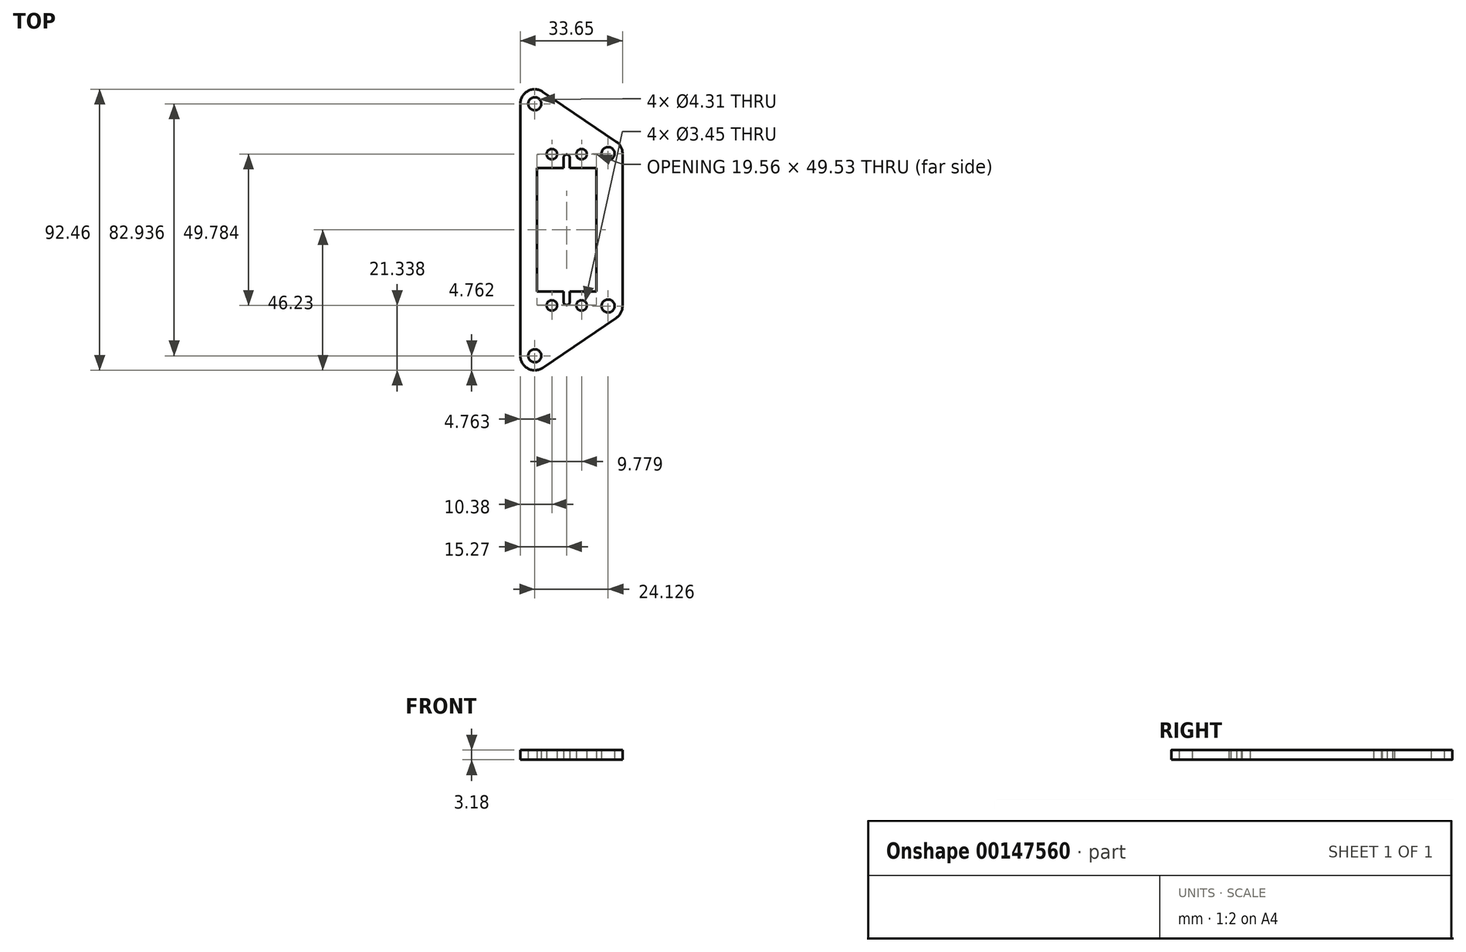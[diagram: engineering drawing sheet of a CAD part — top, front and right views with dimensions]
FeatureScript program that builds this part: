
annotation { "Feature Type Name" : "Feature", "Feature Type Description" : "" }
export const myFeature = defineFeature(function(context is Context, id is Id, definition is map)
    precondition{}
    {
        {
            var Q0;
            Q0=qCreatedBy(makeId("Top.planeOp"),FACE);
            var sketch = newSketch(context, id + "F0", { "sketchPlane" : qUnion([Q0])});
            skLineSegment(sketch, "E0.rect.bottom", {"start": v(-9.78, -20.32) * mm, "end": v(-9.78, 20.32) * mm});
            skLineSegment(sketch, "E0.rect.top", {"start": v(9.78, -20.32) * mm, "end": v(9.78, 20.32) * mm});
            skPoint(sketch, "E0.rect.middle", {"position": v(0, 0) * mm});
            skLineSegment(sketch, "E1.rect.bottom", {"start": v(-4.89, -24.9) * mm, "end": v(-4.89, 24.9) * mm, "construction": true});
            skLineSegment(sketch, "E1.rect.top", {"start": v(4.89, -24.9) * mm, "end": v(4.89, 24.9) * mm, "construction": true});
            skLineSegment(sketch, "E1.rect.left", {"start": v(-4.89, -24.9) * mm, "end": v(4.89, -24.9) * mm, "construction": true});
            skLineSegment(sketch, "E1.rect.right", {"start": v(-4.89, 24.9) * mm, "end": v(4.89, 24.9) * mm, "construction": true});
            skCircle(sketch, "E2", {"center": v(4.89, 24.9) * mm, "radius": 1.73 * mm});
            skCircle(sketch, "E3", {"center": v(-4.89, 24.9) * mm, "radius": 1.73 * mm});
            skCircle(sketch, "E4", {"center": v(4.89, -24.9) * mm, "radius": 1.73 * mm});
            skCircle(sketch, "E5", {"center": v(-4.89, -24.9) * mm, "radius": 1.73 * mm});
            skLineSegment(sketch, "E6", {"start": v(-9.78, 20.32) * mm, "end": v(-1.02, 20.32) * mm});
            skLineSegment(sketch, "E7", {"start": v(-1.02, 20.32) * mm, "end": v(-1.02, 23.75) * mm});
            skLineSegment(sketch, "E8", {"start": v(-1.02, 23.75) * mm, "end": v(1.02, 23.75) * mm, "construction": true});
            skLineSegment(sketch, "E9", {"start": v(1.02, 23.75) * mm, "end": v(1.02, 20.32) * mm});
            skLineSegment(sketch, "E10", {"start": v(1.02, 20.32) * mm, "end": v(9.78, 20.32) * mm});
            skLineSegment(sketch, "E11", {"start": v(9.78, -20.32) * mm, "end": v(1.02, -20.32) * mm});
            skLineSegment(sketch, "E12", {"start": v(1.02, -20.32) * mm, "end": v(1.02, -23.75) * mm});
            skLineSegment(sketch, "E13", {"start": v(1.02, -23.75) * mm, "end": v(-1.02, -23.75) * mm, "construction": true});
            skLineSegment(sketch, "E14", {"start": v(-1.02, -23.75) * mm, "end": v(-1.02, -20.32) * mm});
            skLineSegment(sketch, "E15", {"start": v(-1.02, -20.32) * mm, "end": v(-9.78, -20.32) * mm});
            skArc(sketch, "E16", {"start": v(1.02, 23.75) * mm, "mid": v(0, 24.77) * mm, "end": v(-1.02, 23.75) * mm});
            skArc(sketch, "E17", {"start": v(-1.02, -23.75) * mm, "mid": v(0, -24.76) * mm, "end": v(1.02, -23.75) * mm});
            skLineSegment(sketch, "E18", {"start": v(-1.02, 20.32) * mm, "end": v(1.02, 20.32) * mm, "construction": true});
            skLineSegment(sketch, "E19", {"start": v(0, 20.32) * mm, "end": v(0, 10.9) * mm, "construction": true});
            skLineSegment(sketch, "E20", {"start": v(0, 0) * mm, "end": v(0, 0) * mm});
            skLineSegment(sketch, "E21", {"start": v(13.62, 20.32) * mm, "end": v(13.62, 25.08) * mm, "construction": true});
            skLineSegment(sketch, "E22", {"start": v(9.78, 0) * mm, "end": v(18.38, 0) * mm, "construction": true});
            skCircle(sketch, "E23", {"center": v(13.62, 25.08) * mm, "radius": 2.15 * mm});
            skLineSegment(sketch, "E24", {"start": v(-9.78, 0) * mm, "end": v(-10.5, 0) * mm, "construction": true});
            skLineSegment(sketch, "E25", {"start": v(-10.5, -41.47) * mm, "end": v(-10.5, 41.47) * mm, "construction": true});
            skCircle(sketch, "E26", {"center": v(-10.5, 41.47) * mm, "radius": 2.15 * mm});
            skCircle(sketch, "E27", {"center": v(-10.5, -41.47) * mm, "radius": 2.15 * mm});
            skCircle(sketch, "E28", {"center": v(4.89, 24.9) * mm, "radius": 3.97 * mm, "construction": true});
            skArc(sketch, "E29", {"start": v(18.38, 25.08) * mm, "mid": v(17.83, 27.31) * mm, "end": v(16.3, 29.02) * mm});
            skArc(sketch, "E30", {"start": v(16.3, 29.02) * mm, "mid": v(9.41, 22.85) * mm, "end": v(18.38, 25.08) * mm, "construction": true});
            skLineSegment(sketch, "E31", {"start": v(9.78, 20.32) * mm, "end": v(13.62, 20.32) * mm, "construction": true});
            skLineSegment(sketch, "E32", {"start": v(18.38, 25.08) * mm, "end": v(18.38, -25.08) * mm});
            skArc(sketch, "E33", {"start": v(-7.83, 45.4) * mm, "mid": v(-12.74, 45.68) * mm, "end": v(-15.27, 41.47) * mm});
            skLineSegment(sketch, "E34", {"start": v(-7.83, 45.4) * mm, "end": v(16.3, 29.02) * mm});
            skLineSegment(sketch, "E35", {"start": v(-15.27, 41.47) * mm, "end": v(-15.27, -41.47) * mm});
            skArc(sketch, "E36", {"start": v(16.3, -29.02) * mm, "mid": v(17.83, -27.31) * mm, "end": v(18.38, -25.08) * mm});
            skArc(sketch, "E37", {"start": v(-15.27, -41.47) * mm, "mid": v(-12.74, -45.68) * mm, "end": v(-7.83, -45.4) * mm});
            skLineSegment(sketch, "E38", {"start": v(-7.83, -45.4) * mm, "end": v(16.3, -29.02) * mm});
            skCircle(sketch, "E39", {"center": v(13.62, -25.08) * mm, "radius": 2.15 * mm});
            skSolve(sketch);
        }
        {
            var Q0;
            Q0=qSketchRegion(id+"F0",true);
            extrude(context, id + "F1", {"entities" : qUnion([Q0]), "depth" : 3.17 * mm});
        }
    });
